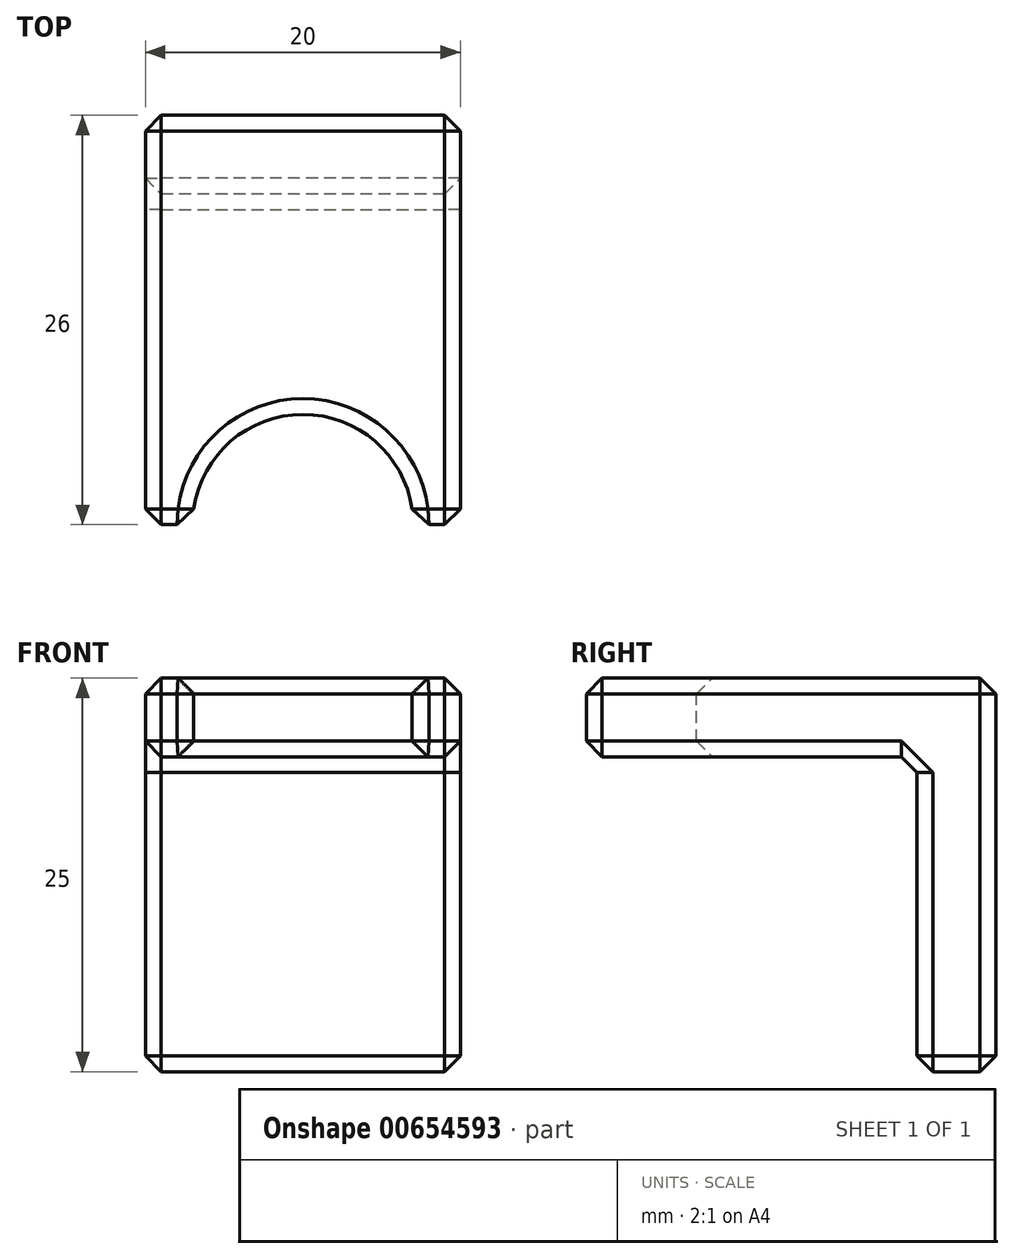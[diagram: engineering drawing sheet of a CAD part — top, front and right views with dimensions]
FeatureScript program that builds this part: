
annotation { "Feature Type Name" : "Feature", "Feature Type Description" : "" }
export const myFeature = defineFeature(function(context is Context, id is Id, definition is map)
    precondition{}
    {
        {
            var Q0;
            Q0=qCreatedBy(makeId("Front.planeOp"),FACE);
            var sketch = newSketch(context, id + "F0", { "sketchPlane" : qUnion([Q0])});
            skLineSegment(sketch, "E0.bottom", {"start": v(0, 0) * mm, "end": v(20, 0) * mm});
            skLineSegment(sketch, "E0.top", {"start": v(0, 25) * mm, "end": v(20, 25) * mm});
            skLineSegment(sketch, "E0.left", {"start": v(0, 0) * mm, "end": v(0, 25) * mm});
            skLineSegment(sketch, "E0.right", {"start": v(20, 0) * mm, "end": v(20, 25) * mm});
            skSolve(sketch);
        }
        {
            var Q0;
            Q0=makeQuery(id+"F0.imprint","IMPRINT",FACE,{"disambiguationData":[TD([[makeQuery(id+"F0.imprint","IMPRINT",EDGE,{"derivedFrom":sQuery(id+"F0.wireOp",EDGE,"E0.bottom")}),1.0]])]});
            extrude(context, id + "F1", {"entities" : qUnion([Q0]), "oppositeDirection" : true, "depth" : 5 * mm, "offsetDistance" : 25 * mm});
        }
        {
            var Q0;
            Q0=makeQuery(id+"F1.opExtrude","CAP_FACE",FACE,{"disambiguationData":[OSD([sQuery(id+"F0.wireOp",EDGE,"E0.bottom"),sQuery(id+"F0.wireOp",EDGE,"E0.top"),sQuery(id+"F0.wireOp",EDGE,"E0.left"),sQuery(id+"F0.wireOp",EDGE,"E0.right")])],"isStart":true});
            var sketch = newSketch(context, id + "F2", { "sketchPlane" : qUnion([Q0])});
            skLineSegment(sketch, "E1.bottom", {"start": v(0, 25) * mm, "end": v(20, 25) * mm});
            skLineSegment(sketch, "E1.top", {"start": v(0, 20) * mm, "end": v(20, 20) * mm});
            skLineSegment(sketch, "E1.left", {"start": v(0, 25) * mm, "end": v(0, 20) * mm});
            skLineSegment(sketch, "E1.right", {"start": v(20, 25) * mm, "end": v(20, 20) * mm});
            skSolve(sketch);
        }
        {
            var Q0;
            Q0=makeQuery(id+"F2.imprint","IMPRINT",FACE,{"disambiguationData":[TD([[makeQuery(id+"F2.imprint","IMPRINT",EDGE,{"derivedFrom":sQuery(id+"F2.wireOp",EDGE,"E1.bottom")}),-1.0]])]});
            extrude(context, id + "F3", {"entities" : qUnion([Q0]), "operationType" : NewBodyOperationType.ADD, "depth" : 30 * mm, "offsetDistance" : 25 * mm});
        }
        {
            var Q0;
            Q0=makeQuery(id+"F3.boolean.opBoolean","MERGE",FACE,{"derivedFrom":[makeQuery(id+"F1.opExtrude","SWEPT_FACE",FACE,{"disambiguationData":[OSD([sQuery(id+"F0.wireOp",EDGE,"E0.top")])]}),makeQuery(id+"F3.opExtrude","SWEPT_FACE",FACE,{"disambiguationData":[OSD([sQuery(id+"F2.wireOp",EDGE,"E1.bottom")])]})]});
            var sketch = newSketch(context, id + "F4", { "sketchPlane" : qUnion([Q0])});
            skArc(sketch, "E2", {"start": v(17, -21) * mm, "mid": v(10, -14) * mm, "end": v(3, -21) * mm});
            skLineSegment(sketch, "E3", {"start": v(3, -21) * mm, "end": v(0, -21) * mm});
            skLineSegment(sketch, "E4", {"start": v(0, -21) * mm, "end": v(0, -30) * mm});
            skLineSegment(sketch, "E5", {"start": v(0, -30) * mm, "end": v(20, -30) * mm});
            skLineSegment(sketch, "E6", {"start": v(20, -30) * mm, "end": v(20, -21) * mm});
            skLineSegment(sketch, "E7", {"start": v(20, -21) * mm, "end": v(17, -21) * mm});
            skSolve(sketch);
        }
        {
            var Q0;
            Q0=makeQuery(id+"F4.imprint","IMPRINT",FACE,{"disambiguationData":[TD([[makeQuery(id+"F4.imprint","IMPRINT",EDGE,{"derivedFrom":sQuery(id+"F4.wireOp",EDGE,"E2")}),1.0]])]});
            extrude(context, id + "F5", {"entities" : qUnion([Q0]), "operationType" : NewBodyOperationType.REMOVE, "endBound" : BoundingType.UP_TO_NEXT, "oppositeDirection" : true, "depth" : 25 * mm, "offsetDistance" : 25 * mm});
        }
        {
            var Q0;
            Q0=makeQuery(id+"F3.opExtrude","CAP_EDGE",EDGE,{"disambiguationData":[OSD([sQuery(id+"F2.wireOp",EDGE,"E1.bottom")])],"isStart":false});
            var Q1;
            Q1=makeQuery(id+"F3.boolean.opBoolean","MERGE",EDGE,{"derivedFrom":[makeQuery(id+"F1.opExtrude","SWEPT_EDGE",EDGE,{"disambiguationData":[OSD([sQuery(id+"F0.wireOp",EDGE,"E0.top"),sQuery(id+"F0.wireOp",EDGE,"E0.right")])]}),makeQuery(id+"F3.opExtrude","SWEPT_EDGE",EDGE,{"disambiguationData":[OSD([sQuery(id+"F2.wireOp",EDGE,"E1.bottom"),sQuery(id+"F2.wireOp",EDGE,"E1.right")])]})]});
            var Q2;
            Q2=makeQuery(id+"F3.boolean.opBoolean","MERGE",EDGE,{"derivedFrom":[makeQuery(id+"F1.opExtrude","SWEPT_EDGE",EDGE,{"disambiguationData":[OSD([sQuery(id+"F0.wireOp",EDGE,"E0.top"),sQuery(id+"F0.wireOp",EDGE,"E0.left")])]}),makeQuery(id+"F3.opExtrude","SWEPT_EDGE",EDGE,{"disambiguationData":[OSD([sQuery(id+"F2.wireOp",EDGE,"E1.bottom"),sQuery(id+"F2.wireOp",EDGE,"E1.left")])]})]});
            var Q3;
            Q3=makeQuery(id+"F1.opExtrude","CAP_EDGE",EDGE,{"disambiguationData":[OSD([sQuery(id+"F0.wireOp",EDGE,"E0.top")])],"isStart":false});
            var Q4;
            Q4=makeQuery(id+"F3.opExtrude","CAP_FACE",FACE,{"disambiguationData":[OSD([sQuery(id+"F2.wireOp",EDGE,"E1.bottom"),sQuery(id+"F2.wireOp",EDGE,"E1.top"),sQuery(id+"F2.wireOp",EDGE,"E1.left"),sQuery(id+"F2.wireOp",EDGE,"E1.right")])],"isStart":false});
            var Q5;
            Q5=makeQuery(id+"F3.boolean.opBoolean","MERGE",FACE,{"derivedFrom":[makeQuery(id+"F1.opExtrude","SWEPT_FACE",FACE,{"disambiguationData":[OSD([sQuery(id+"F0.wireOp",EDGE,"E0.left")])]}),makeQuery(id+"F3.opExtrude","SWEPT_FACE",FACE,{"disambiguationData":[OSD([sQuery(id+"F2.wireOp",EDGE,"E1.left")])]})]});
            var Q6;
            Q6=makeQuery(id+"F1.opExtrude","CAP_FACE",FACE,{"disambiguationData":[OSD([sQuery(id+"F0.wireOp",EDGE,"E0.bottom"),sQuery(id+"F0.wireOp",EDGE,"E0.top"),sQuery(id+"F0.wireOp",EDGE,"E0.left"),sQuery(id+"F0.wireOp",EDGE,"E0.right")])],"isStart":true});
            var Q7;
            Q7=makeQuery(id+"F3.boolean.opBoolean","MERGE",FACE,{"derivedFrom":[makeQuery(id+"F1.opExtrude","SWEPT_FACE",FACE,{"disambiguationData":[OSD([sQuery(id+"F0.wireOp",EDGE,"E0.right")])]}),makeQuery(id+"F3.opExtrude","SWEPT_FACE",FACE,{"disambiguationData":[OSD([sQuery(id+"F2.wireOp",EDGE,"E1.right")])]})]});
            var Q8;
            Q8=makeQuery(id+"F1.opExtrude","SWEPT_FACE",FACE,{"disambiguationData":[OSD([sQuery(id+"F0.wireOp",EDGE,"E0.bottom")])]});
            var Q9;
            Q9=makeQuery(id+"F5.boolean.opBoolean","COPY",FACE,{"derivedFrom":makeQuery(id+"F5.opExtrude","SWEPT_FACE",FACE,{"disambiguationData":[OSD([sQuery(id+"F4.wireOp",EDGE,"E2")])]})});
            var Q10;
            Q10=makeQuery(id+"F5.boolean.opBoolean","COPY",FACE,{"derivedFrom":makeQuery(id+"F5.opExtrude","SWEPT_FACE",FACE,{"disambiguationData":[OSD([sQuery(id+"F4.wireOp",EDGE,"E7")])]})});
            var Q11;
            Q11=makeQuery(id+"F5.boolean.opBoolean","COPY",FACE,{"derivedFrom":makeQuery(id+"F5.opExtrude","SWEPT_FACE",FACE,{"disambiguationData":[OSD([sQuery(id+"F4.wireOp",EDGE,"E3")])]})});
            chamfer(context, id + "F6", {"entities" : qUnion([Q0, Q1, Q2, Q3, Q4, Q5, Q6, Q7, Q8, Q9, Q10, Q11]), "width" : 1 * mm, "tangentPropagation" : true});
        }
    });
